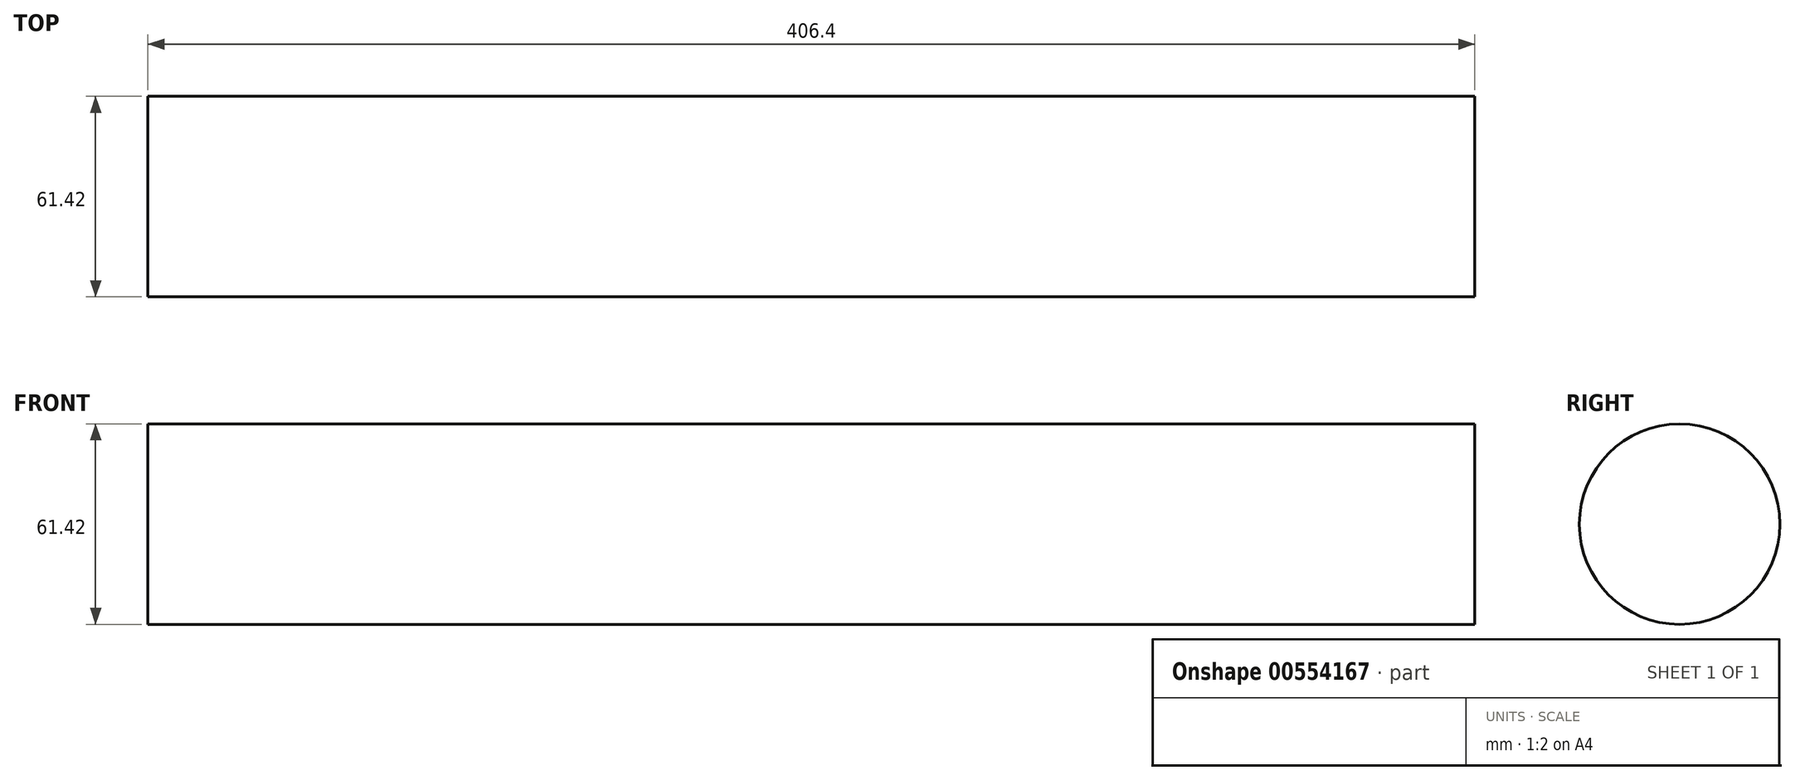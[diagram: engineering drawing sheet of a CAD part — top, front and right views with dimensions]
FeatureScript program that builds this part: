
annotation { "Feature Type Name" : "Feature", "Feature Type Description" : "" }
export const myFeature = defineFeature(function(context is Context, id is Id, definition is map)
    precondition{}
    {
        {
            var Q0;
            Q0=qCreatedBy(makeId("Right.planeOp"),FACE);
            var sketch = newSketch(context, id + "F0", { "sketchPlane" : qUnion([Q0])});
            skCircle(sketch, "E0", {"center": v(0, 0) * mm, "radius": 30.7 * mm});
            skSolve(sketch);
        }
        {
            var Q0;
            Q0 = qSketchRegion(id + "F0", true);
            extrude(context, id + "F1", {"entities" : qUnion([Q0]), "depth" : 406.4 * mm, "offsetDistance" : 25.4 * mm});
        }
    });
